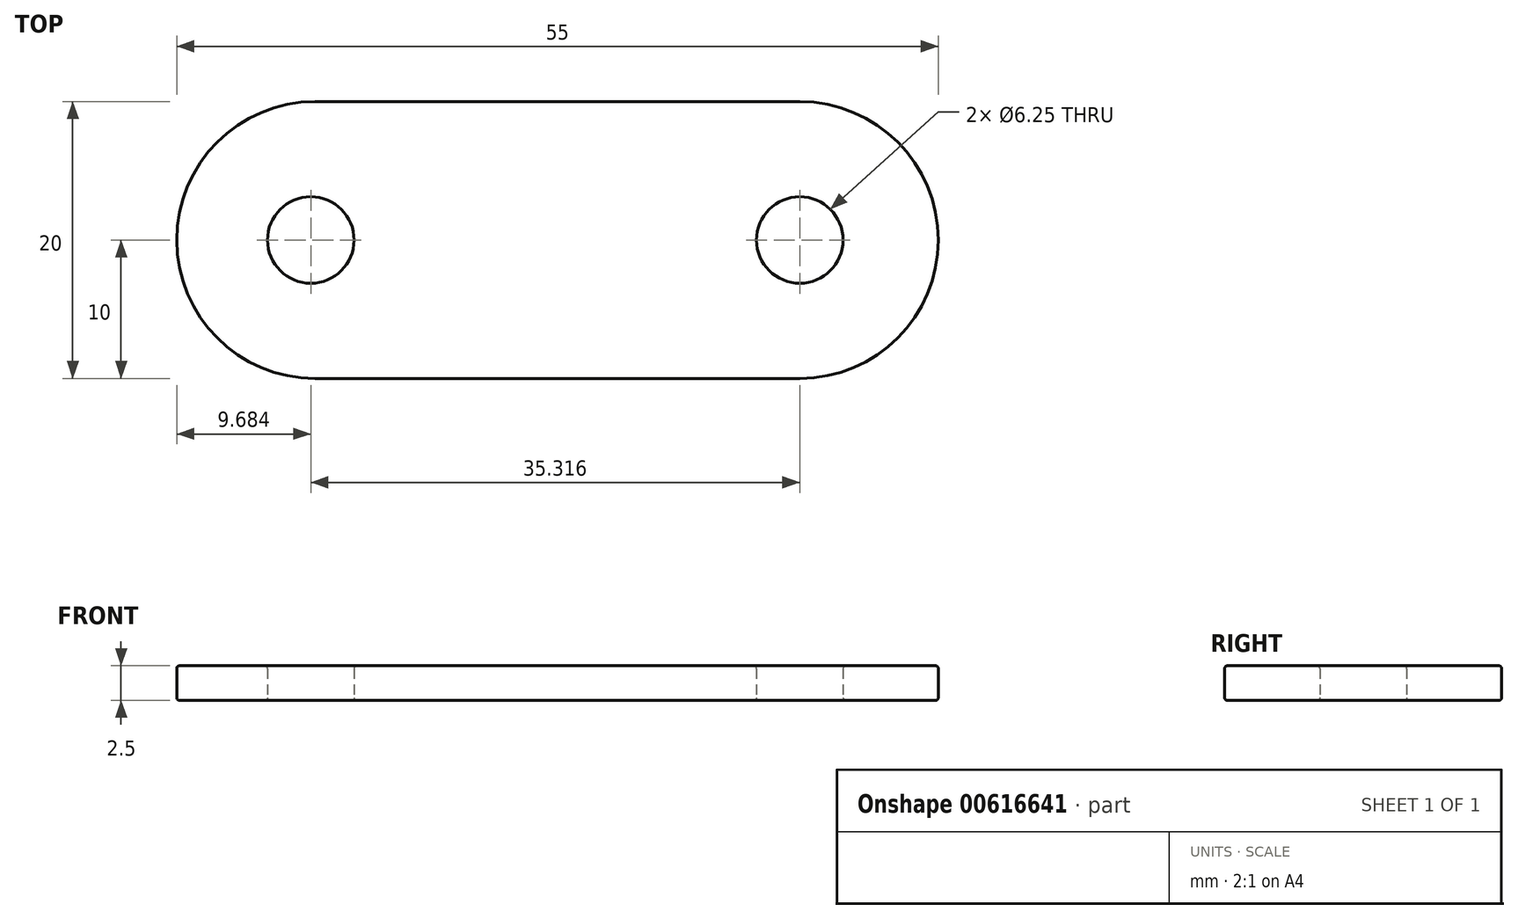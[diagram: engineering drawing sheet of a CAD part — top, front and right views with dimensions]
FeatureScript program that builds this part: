
annotation { "Feature Type Name" : "Feature", "Feature Type Description" : "" }
export const myFeature = defineFeature(function(context is Context, id is Id, definition is map)
    precondition{}
    {
        {
            var Q0;
            Q0=qCreatedBy(makeId("Top.planeOp"),FACE);
            var sketch = newSketch(context, id + "F0", { "sketchPlane" : qUnion([Q0])});
            skLineSegment(sketch, "E0.bottom", {"start": v(17.5, -10) * mm, "end": v(-17.5, -10) * mm});
            skLineSegment(sketch, "E0.top", {"start": v(17.5, 10) * mm, "end": v(-17.5, 10) * mm});
            skLineSegment(sketch, "E0.left", {"start": v(27.5, 0) * mm, "end": v(27.5, 0) * mm});
            skLineSegment(sketch, "E0.right", {"start": v(-27.5, 0) * mm, "end": v(-27.5, 0) * mm});
            skPoint(sketch, "E0.middle", {"position": v(0, 0) * mm});
            skPoint(sketch, "E1.visualSharp", {"position": v(-27.5, 10) * mm});
            skArc(sketch, "E1.filletArc", {"start": v(-17.5, 10) * mm, "mid": v(-24.57, 7.07) * mm, "end": v(-27.5, 0) * mm});
            skPoint(sketch, "E2.visualSharp", {"position": v(-27.5, -10) * mm});
            skArc(sketch, "E2.filletArc", {"start": v(-27.5, 0) * mm, "mid": v(-24.57, -7.07) * mm, "end": v(-17.5, -10) * mm});
            skPoint(sketch, "E3.visualSharp", {"position": v(27.5, -10) * mm});
            skArc(sketch, "E3.filletArc", {"start": v(17.5, -10) * mm, "mid": v(24.57, -7.07) * mm, "end": v(27.5, 0) * mm});
            skPoint(sketch, "E4.visualSharp", {"position": v(27.5, 10) * mm});
            skArc(sketch, "E4.filletArc", {"start": v(27.5, 0) * mm, "mid": v(24.57, 7.07) * mm, "end": v(17.5, 10) * mm});
            skCircle(sketch, "E5", {"center": v(-17.82, 0) * mm, "radius": 3.12 * mm});
            skCircle(sketch, "E6", {"center": v(17.5, 0) * mm, "radius": 3.12 * mm});
            skSolve(sketch);
        }
        {
            var Q0;
            Q0=makeQuery(id+"F0.imprint","IMPRINT",FACE,{"disambiguationData":[TD([[makeQuery(id+"F0.imprint","IMPRINT",EDGE,{"derivedFrom":sQuery(id+"F0.wireOp",EDGE,"E0.bottom")}),-1.0]])]});
            extrude(context, id + "F1", {"entities" : qUnion([Q0]), "depth" : 2.5 * mm, "offsetDistance" : 25 * mm});
        }
        {
            var Q0;
            Q0=makeQuery(id+"F1.opExtrude","CAP_EDGE",EDGE,{"disambiguationData":[OSD([sQuery(id+"F0.wireOp",EDGE,"E1.filletArc"),sQuery(id+"F0.wireOp",EDGE,"E2.filletArc")])],"isStart":false});
            var Q1;
            Q1=makeQuery(id+"F1.opExtrude","CAP_EDGE",EDGE,{"disambiguationData":[OSD([sQuery(id+"F0.wireOp",EDGE,"E0.top")])],"isStart":false});
            var Q2;
            Q2=makeQuery(id+"F1.opExtrude","CAP_EDGE",EDGE,{"disambiguationData":[OSD([sQuery(id+"F0.wireOp",EDGE,"E3.filletArc"),sQuery(id+"F0.wireOp",EDGE,"E4.filletArc")])],"isStart":false});
            var Q3;
            Q3=makeQuery(id+"F1.opExtrude","CAP_FACE",FACE,{"disambiguationData":[OSD([sQuery(id+"F0.wireOp",EDGE,"E0.bottom"),sQuery(id+"F0.wireOp",EDGE,"E0.top"),sQuery(id+"F0.wireOp",EDGE,"E1.filletArc"),sQuery(id+"F0.wireOp",EDGE,"E2.filletArc"),sQuery(id+"F0.wireOp",EDGE,"E3.filletArc"),sQuery(id+"F0.wireOp",EDGE,"E4.filletArc"),sQuery(id+"F0.wireOp",EDGE,"E5"),sQuery(id+"F0.wireOp",EDGE,"E6")])],"isStart":false});
            var Q4;
            Q4=makeQuery(id+"F1.opExtrude","CAP_EDGE",EDGE,{"disambiguationData":[OSD([sQuery(id+"F0.wireOp",EDGE,"E5")])],"isStart":false});
            var Q5;
            Q5=makeQuery(id+"F1.opExtrude","CAP_EDGE",EDGE,{"disambiguationData":[OSD([sQuery(id+"F0.wireOp",EDGE,"E6")])],"isStart":false});
            var Q6;
            Q6=makeQuery(id+"F1.opExtrude","CAP_EDGE",EDGE,{"disambiguationData":[OSD([sQuery(id+"F0.wireOp",EDGE,"E5")])],"isStart":true});
            var Q7;
            Q7=makeQuery(id+"F1.opExtrude","CAP_EDGE",EDGE,{"disambiguationData":[OSD([sQuery(id+"F0.wireOp",EDGE,"E6")])],"isStart":true});
            var Q8;
            Q8=makeQuery(id+"F1.opExtrude","CAP_EDGE",EDGE,{"disambiguationData":[OSD([sQuery(id+"F0.wireOp",EDGE,"E3.filletArc"),sQuery(id+"F0.wireOp",EDGE,"E4.filletArc")])],"isStart":true});
            var Q9;
            Q9=makeQuery(id+"F1.opExtrude","CAP_EDGE",EDGE,{"disambiguationData":[OSD([sQuery(id+"F0.wireOp",EDGE,"E0.bottom")])],"isStart":true});
            var Q10;
            Q10=makeQuery(id+"F1.opExtrude","CAP_EDGE",EDGE,{"disambiguationData":[OSD([sQuery(id+"F0.wireOp",EDGE,"E1.filletArc"),sQuery(id+"F0.wireOp",EDGE,"E2.filletArc")])],"isStart":true});
            var Q11;
            Q11=makeQuery(id+"F1.opExtrude","CAP_EDGE",EDGE,{"disambiguationData":[OSD([sQuery(id+"F0.wireOp",EDGE,"E0.top")])],"isStart":true});
            fillet(context, id + "F2", {"entities" : qUnion([Q0, Q1, Q2, Q3, Q4, Q5, Q6, Q7, Q8, Q9, Q10, Q11]), "radius" : 0.2 * mm, "tangentPropagation" : true, "allowEdgeOverflow" : false});
        }
    });
